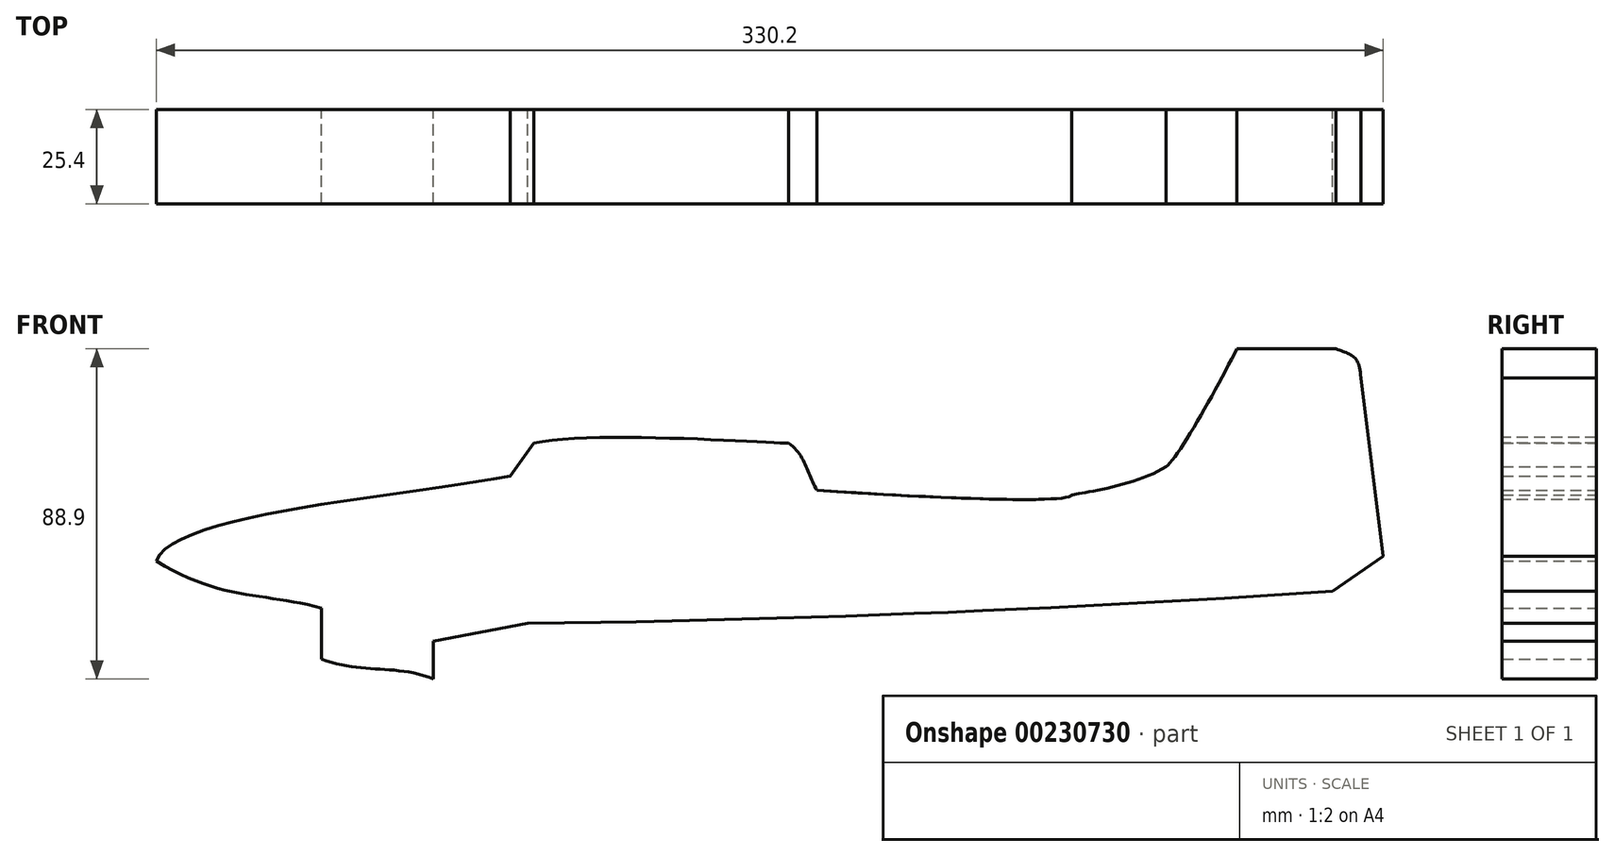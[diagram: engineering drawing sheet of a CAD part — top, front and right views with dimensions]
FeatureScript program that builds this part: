
annotation { "Feature Type Name" : "Feature", "Feature Type Description" : "" }
export const myFeature = defineFeature(function(context is Context, id is Id, definition is map)
    precondition{}
    {
        {
            var Q0;
            Q0=qCreatedBy(makeId("Front.planeOp"),FACE);
            var sketch = newSketch(context, id + "F0", { "sketchPlane" : qUnion([Q0])});
            skPoint(sketch, "E0.middle", {"position": v(0, 0) * mm});
            skFitSpline(sketch, "E1", {"points": [v(-165.1, -12.7) * mm, v(-69.85, 10.16) * mm], "startDerivative": vector(13.33, 38.1) * mm, "endDerivative": vector(100.47, 18.15) * mm});
            skLineSegment(sketch, "E2", {"start": v(-69.85, 10.16) * mm, "end": v(-63.5, 19.05) * mm});
            skFitSpline(sketch, "E3", {"points": [v(-63.5, 19.05) * mm, v(5.08, 19.05) * mm], "startDerivative": vector(49.07, 10.36) * mm, "endDerivative": vector(15.51, 0.13) * mm});
            skFitSpline(sketch, "E4", {"points": [v(5.08, 19.05) * mm, v(12.7, 6.35) * mm], "startDerivative": vector(14.02, -9.98) * mm, "endDerivative": vector(7.62, -12.7) * mm});
            skFitSpline(sketch, "E5", {"points": [v(12.7, 6.35) * mm, v(81.28, 5.08) * mm], "startDerivative": vector(125.13, -8.3) * mm, "endDerivative": vector(2.67, 6.07) * mm});
            skFitSpline(sketch, "E6", {"points": [v(81.28, 5.08) * mm, v(106.68, 12.7) * mm], "startDerivative": vector(4.48, 1.09) * mm, "endDerivative": vector(24.08, 15.56) * mm});
            skFitSpline(sketch, "E7", {"points": [v(106.68, 12.7) * mm, v(125.73, 44.45) * mm], "startDerivative": vector(10.18, 7.13) * mm, "endDerivative": vector(15.33, 30.35) * mm});
            skLineSegment(sketch, "E8", {"start": v(125.73, 44.45) * mm, "end": v(152.4, 44.45) * mm});
            skFitSpline(sketch, "E9", {"points": [v(152.4, 44.45) * mm, v(159.08, 36.65) * mm], "startDerivative": vector(11.43, -4.49) * mm, "endDerivative": vector(0.28, -18.36) * mm});
            skLineSegment(sketch, "E10", {"start": v(159.08, 36.65) * mm, "end": v(165.1, -11.43) * mm});
            skLineSegment(sketch, "E11", {"start": v(165.1, -11.43) * mm, "end": v(151.45, -20.84) * mm});
            skFitSpline(sketch, "E12", {"points": [v(151.45, -20.84) * mm, v(-65.1, -29.48) * mm], "startDerivative": vector(-225.65, -14.85) * mm, "endDerivative": vector(-227.64, -2.83) * mm});
            skLineSegment(sketch, "E13", {"start": v(-90.5, -44.45) * mm, "end": v(-90.5, -34.3) * mm});
            skLineSegment(sketch, "E14", {"start": v(-90.5, -34.3) * mm, "end": v(-65.1, -29.48) * mm});
            skFitSpline(sketch, "E15", {"points": [v(-120.63, -39.12) * mm, v(-90.5, -44.45) * mm], "startDerivative": vector(32.05, -12.26) * mm, "endDerivative": vector(31.64, -12.5) * mm});
            skLineSegment(sketch, "E16", {"start": v(-120.63, -39.12) * mm, "end": v(-120.63, -25.4) * mm});
            skFitSpline(sketch, "E17", {"points": [v(-165.1, -12.7) * mm, v(-120.63, -25.4) * mm], "startDerivative": vector(51.73, -32.28) * mm, "endDerivative": vector(44.47, -12.7) * mm});
            skSolve(sketch);
        }
        {
            var Q0;
            Q0 = qSketchRegion(id + "F0", true);
            extrude(context, id + "F1", {"entities" : qUnion([Q0]), "depth" : 25.4 * mm});
        }
    });
